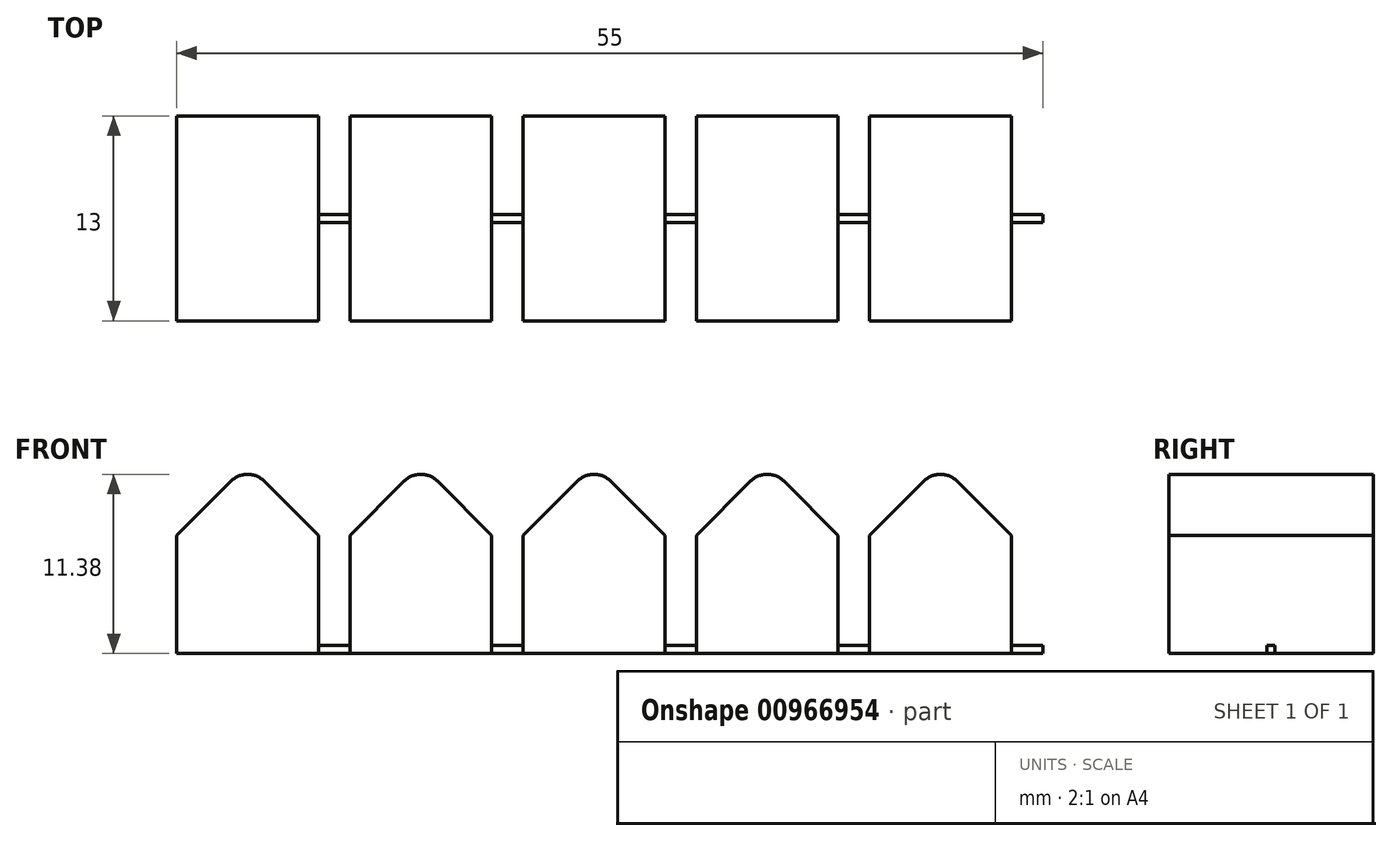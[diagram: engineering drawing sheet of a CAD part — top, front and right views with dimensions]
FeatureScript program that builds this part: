
annotation { "Feature Type Name" : "Feature", "Feature Type Description" : "" }
export const myFeature = defineFeature(function(context is Context, id is Id, definition is map)
    precondition{}
    {
        {
            var Q0;
            Q0=qCreatedBy(makeId("Front.planeOp"),FACE);
            var sketch = newSketch(context, id + "F0", { "sketchPlane" : qUnion([Q0])});
            skLineSegment(sketch, "E0.bottom", {"start": v(4.5, -3.75) * mm, "end": v(-4.5, -3.75) * mm});
            skLineSegment(sketch, "E0.top", {"start": v(4.5, 3.75) * mm, "end": v(-4.5, 3.75) * mm});
            skLineSegment(sketch, "E0.left", {"start": v(4.5, -3.75) * mm, "end": v(4.5, 3.75) * mm});
            skLineSegment(sketch, "E0.right", {"start": v(-4.5, -3.75) * mm, "end": v(-4.5, 3.75) * mm});
            skPoint(sketch, "E0.middle", {"position": v(0, 0) * mm});
            skLineSegment(sketch, "E1", {"start": v(-4.5, 3.75) * mm, "end": v(-1.06, 7.19) * mm});
            skLineSegment(sketch, "E2", {"start": v(1.06, 7.19) * mm, "end": v(4.5, 3.75) * mm});
            skPoint(sketch, "E3.visualSharp", {"position": v(0, 8.25) * mm});
            skArc(sketch, "E3.filletArc", {"start": v(1.06, 7.19) * mm, "mid": v(0, 7.63) * mm, "end": v(-1.06, 7.19) * mm});
            skLineSegment(sketch, "E4.bottom", {"start": v(4.5, -3.75) * mm, "end": v(6.5, -3.75) * mm});
            skLineSegment(sketch, "E4.top", {"start": v(4.5, -3.25) * mm, "end": v(6.5, -3.25) * mm});
            skLineSegment(sketch, "E4.left", {"start": v(4.5, -3.75) * mm, "end": v(4.5, -3.25) * mm});
            skLineSegment(sketch, "E4.right", {"start": v(6.5, -3.75) * mm, "end": v(6.5, -3.25) * mm});
            skLineSegment(sketch, "E5.1.0.0", {"start": v(12.06, 7.19) * mm, "end": v(15.5, 3.75) * mm});
            skLineSegment(sketch, "E5.1.0.1", {"start": v(15.5, -3.75) * mm, "end": v(15.5, 3.75) * mm});
            skLineSegment(sketch, "E5.1.0.2", {"start": v(15.5, -3.75) * mm, "end": v(17.5, -3.75) * mm});
            skLineSegment(sketch, "E5.1.0.3", {"start": v(15.5, 3.75) * mm, "end": v(6.5, 3.75) * mm});
            skPoint(sketch, "E5.1.0.4", {"position": v(11, 8.25) * mm});
            skArc(sketch, "E5.1.0.5", {"start": v(12.06, 7.19) * mm, "mid": v(11, 7.63) * mm, "end": v(9.94, 7.19) * mm});
            skLineSegment(sketch, "E5.1.0.6", {"start": v(15.5, -3.75) * mm, "end": v(6.5, -3.75) * mm});
            skLineSegment(sketch, "E5.1.0.7", {"start": v(15.5, -3.25) * mm, "end": v(17.5, -3.25) * mm});
            skLineSegment(sketch, "E5.1.0.8", {"start": v(6.5, -3.75) * mm, "end": v(6.5, 3.75) * mm});
            skLineSegment(sketch, "E5.1.0.9", {"start": v(6.5, 3.75) * mm, "end": v(9.94, 7.19) * mm});
            skPoint(sketch, "E5.1.0.10", {"position": v(11, 0) * mm});
            skLineSegment(sketch, "E5.1.0.11", {"start": v(15.5, -3.75) * mm, "end": v(15.5, -3.25) * mm});
            skLineSegment(sketch, "E5.1.0.12", {"start": v(17.5, -3.75) * mm, "end": v(17.5, -3.25) * mm});
            skLineSegment(sketch, "E5.2.0.0", {"start": v(23.06, 7.19) * mm, "end": v(26.5, 3.75) * mm});
            skLineSegment(sketch, "E5.2.0.1", {"start": v(26.5, -3.75) * mm, "end": v(26.5, 3.75) * mm});
            skLineSegment(sketch, "E5.2.0.2", {"start": v(26.5, -3.75) * mm, "end": v(28.5, -3.75) * mm});
            skLineSegment(sketch, "E5.2.0.3", {"start": v(26.5, 3.75) * mm, "end": v(17.5, 3.75) * mm});
            skPoint(sketch, "E5.2.0.4", {"position": v(22, 8.25) * mm});
            skArc(sketch, "E5.2.0.5", {"start": v(23.06, 7.19) * mm, "mid": v(22, 7.63) * mm, "end": v(20.94, 7.19) * mm});
            skLineSegment(sketch, "E5.2.0.6", {"start": v(26.5, -3.75) * mm, "end": v(17.5, -3.75) * mm});
            skLineSegment(sketch, "E5.2.0.7", {"start": v(26.5, -3.25) * mm, "end": v(28.5, -3.25) * mm});
            skLineSegment(sketch, "E5.2.0.8", {"start": v(17.5, -3.75) * mm, "end": v(17.5, 3.75) * mm});
            skLineSegment(sketch, "E5.2.0.9", {"start": v(17.5, 3.75) * mm, "end": v(20.94, 7.19) * mm});
            skPoint(sketch, "E5.2.0.10", {"position": v(22, 0) * mm});
            skLineSegment(sketch, "E5.2.0.11", {"start": v(26.5, -3.75) * mm, "end": v(26.5, -3.25) * mm});
            skLineSegment(sketch, "E5.2.0.12", {"start": v(28.5, -3.75) * mm, "end": v(28.5, -3.25) * mm});
            skLineSegment(sketch, "E5.3.0.0", {"start": v(34.06, 7.19) * mm, "end": v(37.5, 3.75) * mm});
            skLineSegment(sketch, "E5.3.0.1", {"start": v(37.5, -3.75) * mm, "end": v(37.5, 3.75) * mm});
            skLineSegment(sketch, "E5.3.0.2", {"start": v(37.5, -3.75) * mm, "end": v(39.5, -3.75) * mm});
            skLineSegment(sketch, "E5.3.0.3", {"start": v(37.5, 3.75) * mm, "end": v(28.5, 3.75) * mm});
            skPoint(sketch, "E5.3.0.4", {"position": v(33, 8.25) * mm});
            skArc(sketch, "E5.3.0.5", {"start": v(34.06, 7.19) * mm, "mid": v(33, 7.63) * mm, "end": v(31.94, 7.19) * mm});
            skLineSegment(sketch, "E5.3.0.6", {"start": v(37.5, -3.75) * mm, "end": v(28.5, -3.75) * mm});
            skLineSegment(sketch, "E5.3.0.7", {"start": v(37.5, -3.25) * mm, "end": v(39.5, -3.25) * mm});
            skLineSegment(sketch, "E5.3.0.8", {"start": v(28.5, -3.75) * mm, "end": v(28.5, 3.75) * mm});
            skLineSegment(sketch, "E5.3.0.9", {"start": v(28.5, 3.75) * mm, "end": v(31.94, 7.19) * mm});
            skPoint(sketch, "E5.3.0.10", {"position": v(33, 0) * mm});
            skLineSegment(sketch, "E5.3.0.11", {"start": v(37.5, -3.75) * mm, "end": v(37.5, -3.25) * mm});
            skLineSegment(sketch, "E5.3.0.12", {"start": v(39.5, -3.75) * mm, "end": v(39.5, -3.25) * mm});
            skLineSegment(sketch, "E5.4.0.0", {"start": v(45.06, 7.19) * mm, "end": v(48.5, 3.75) * mm});
            skLineSegment(sketch, "E5.4.0.1", {"start": v(48.5, -3.75) * mm, "end": v(48.5, 3.75) * mm});
            skLineSegment(sketch, "E5.4.0.2", {"start": v(48.5, -3.75) * mm, "end": v(50.5, -3.75) * mm});
            skLineSegment(sketch, "E5.4.0.3", {"start": v(48.5, 3.75) * mm, "end": v(39.5, 3.75) * mm});
            skPoint(sketch, "E5.4.0.4", {"position": v(44, 8.25) * mm});
            skArc(sketch, "E5.4.0.5", {"start": v(45.06, 7.19) * mm, "mid": v(44, 7.63) * mm, "end": v(42.94, 7.19) * mm});
            skLineSegment(sketch, "E5.4.0.6", {"start": v(48.5, -3.75) * mm, "end": v(39.5, -3.75) * mm});
            skLineSegment(sketch, "E5.4.0.7", {"start": v(48.5, -3.25) * mm, "end": v(50.5, -3.25) * mm});
            skLineSegment(sketch, "E5.4.0.8", {"start": v(39.5, -3.75) * mm, "end": v(39.5, 3.75) * mm});
            skLineSegment(sketch, "E5.4.0.9", {"start": v(39.5, 3.75) * mm, "end": v(42.94, 7.19) * mm});
            skPoint(sketch, "E5.4.0.10", {"position": v(44, 0) * mm});
            skLineSegment(sketch, "E5.4.0.11", {"start": v(48.5, -3.75) * mm, "end": v(48.5, -3.25) * mm});
            skLineSegment(sketch, "E5.4.0.12", {"start": v(50.5, -3.75) * mm, "end": v(50.5, -3.25) * mm});
            skLineSegment(sketch, "E5.direction1", {"start": v(-4.5, -3.75) * mm, "end": v(6.5, -3.75) * mm, "construction": true});
            skSolve(sketch);
        }
        {
            var Q0;
            Q0 = qSketchRegion(id + "F0", true);
            extrude(context, id + "F1", {"entities" : qUnion([Q0]), "oppositeDirection" : true, "depth" : 13 * mm, "offsetDistance" : 25 * mm});
        }
        {
            var Q0;
            Q0=makeQuery(id+"F1.opExtrude","SWEPT_FACE",FACE,{"disambiguationData":[OSD([sQuery(id+"F0.wireOp",EDGE,"E0.bottom"),sQuery(id+"F0.wireOp",EDGE,"E4.bottom"),sQuery(id+"F0.wireOp",EDGE,"E5.1.0.2"),sQuery(id+"F0.wireOp",EDGE,"E5.1.0.6"),sQuery(id+"F0.wireOp",EDGE,"E5.2.0.2"),sQuery(id+"F0.wireOp",EDGE,"E5.2.0.6"),sQuery(id+"F0.wireOp",EDGE,"E5.3.0.2"),sQuery(id+"F0.wireOp",EDGE,"E5.3.0.6"),sQuery(id+"F0.wireOp",EDGE,"E5.4.0.2"),sQuery(id+"F0.wireOp",EDGE,"E5.4.0.6")])]});
            var sketch = newSketch(context, id + "F2", { "sketchPlane" : qUnion([Q0])});
            skPoint(sketch, "E6", {"position": v(4.5, 0) * mm});
            skLineSegment(sketch, "E7.bottom", {"start": v(4.5, 0) * mm, "end": v(6.5, 0) * mm});
            skLineSegment(sketch, "E7.top", {"start": v(4.5, -6.25) * mm, "end": v(6.5, -6.25) * mm});
            skLineSegment(sketch, "E7.left", {"start": v(4.5, 0) * mm, "end": v(4.5, -6.25) * mm});
            skLineSegment(sketch, "E7.right", {"start": v(6.5, 0) * mm, "end": v(6.5, -6.25) * mm});
            skLineSegment(sketch, "E8.0.1.0", {"start": v(4.5, -6.75) * mm, "end": v(6.5, -6.75) * mm});
            skLineSegment(sketch, "E8.0.1.1", {"start": v(6.5, -6.75) * mm, "end": v(6.5, -13) * mm});
            skPoint(sketch, "E8.0.1.2", {"position": v(4.5, -6.75) * mm});
            skLineSegment(sketch, "E8.0.1.3", {"start": v(4.5, -6.75) * mm, "end": v(4.5, -13) * mm});
            skLineSegment(sketch, "E8.0.1.4", {"start": v(4.5, -13) * mm, "end": v(6.5, -13) * mm});
            skLineSegment(sketch, "E8.1.0.0", {"start": v(15.5, 0) * mm, "end": v(17.5, 0) * mm});
            skLineSegment(sketch, "E8.1.0.1", {"start": v(17.5, 0) * mm, "end": v(17.5, -6.25) * mm});
            skPoint(sketch, "E8.1.0.2", {"position": v(15.5, 0) * mm});
            skLineSegment(sketch, "E8.1.0.3", {"start": v(15.5, 0) * mm, "end": v(15.5, -6.25) * mm});
            skLineSegment(sketch, "E8.1.0.4", {"start": v(15.5, -6.25) * mm, "end": v(17.5, -6.25) * mm});
            skLineSegment(sketch, "E8.1.1.0", {"start": v(15.5, -6.75) * mm, "end": v(17.5, -6.75) * mm});
            skLineSegment(sketch, "E8.1.1.1", {"start": v(17.5, -6.75) * mm, "end": v(17.5, -13) * mm});
            skPoint(sketch, "E8.1.1.2", {"position": v(15.5, -6.75) * mm});
            skLineSegment(sketch, "E8.1.1.3", {"start": v(15.5, -6.75) * mm, "end": v(15.5, -13) * mm});
            skLineSegment(sketch, "E8.1.1.4", {"start": v(15.5, -13) * mm, "end": v(17.5, -13) * mm});
            skLineSegment(sketch, "E8.2.0.0", {"start": v(26.5, 0) * mm, "end": v(28.5, 0) * mm});
            skLineSegment(sketch, "E8.2.0.1", {"start": v(28.5, 0) * mm, "end": v(28.5, -6.25) * mm});
            skPoint(sketch, "E8.2.0.2", {"position": v(26.5, 0) * mm});
            skLineSegment(sketch, "E8.2.0.3", {"start": v(26.5, 0) * mm, "end": v(26.5, -6.25) * mm});
            skLineSegment(sketch, "E8.2.0.4", {"start": v(26.5, -6.25) * mm, "end": v(28.5, -6.25) * mm});
            skLineSegment(sketch, "E8.2.1.0", {"start": v(26.5, -6.75) * mm, "end": v(28.5, -6.75) * mm});
            skLineSegment(sketch, "E8.2.1.1", {"start": v(28.5, -6.75) * mm, "end": v(28.5, -13) * mm});
            skPoint(sketch, "E8.2.1.2", {"position": v(26.5, -6.75) * mm});
            skLineSegment(sketch, "E8.2.1.3", {"start": v(26.5, -6.75) * mm, "end": v(26.5, -13) * mm});
            skLineSegment(sketch, "E8.2.1.4", {"start": v(26.5, -13) * mm, "end": v(28.5, -13) * mm});
            skLineSegment(sketch, "E8.3.0.0", {"start": v(37.5, 0) * mm, "end": v(39.5, 0) * mm});
            skLineSegment(sketch, "E8.3.0.1", {"start": v(39.5, 0) * mm, "end": v(39.5, -6.25) * mm});
            skPoint(sketch, "E8.3.0.2", {"position": v(37.5, 0) * mm});
            skLineSegment(sketch, "E8.3.0.3", {"start": v(37.5, 0) * mm, "end": v(37.5, -6.25) * mm});
            skLineSegment(sketch, "E8.3.0.4", {"start": v(37.5, -6.25) * mm, "end": v(39.5, -6.25) * mm});
            skLineSegment(sketch, "E8.3.1.0", {"start": v(37.5, -6.75) * mm, "end": v(39.5, -6.75) * mm});
            skLineSegment(sketch, "E8.3.1.1", {"start": v(39.5, -6.75) * mm, "end": v(39.5, -13) * mm});
            skPoint(sketch, "E8.3.1.2", {"position": v(37.5, -6.75) * mm});
            skLineSegment(sketch, "E8.3.1.3", {"start": v(37.5, -6.75) * mm, "end": v(37.5, -13) * mm});
            skLineSegment(sketch, "E8.3.1.4", {"start": v(37.5, -13) * mm, "end": v(39.5, -13) * mm});
            skLineSegment(sketch, "E8.4.0.0", {"start": v(48.5, 0) * mm, "end": v(50.5, 0) * mm});
            skLineSegment(sketch, "E8.4.0.1", {"start": v(50.5, 0) * mm, "end": v(50.5, -6.25) * mm});
            skPoint(sketch, "E8.4.0.2", {"position": v(48.5, 0) * mm});
            skLineSegment(sketch, "E8.4.0.3", {"start": v(48.5, 0) * mm, "end": v(48.5, -6.25) * mm});
            skLineSegment(sketch, "E8.4.0.4", {"start": v(48.5, -6.25) * mm, "end": v(50.5, -6.25) * mm});
            skLineSegment(sketch, "E8.4.1.0", {"start": v(48.5, -6.75) * mm, "end": v(50.5, -6.75) * mm});
            skLineSegment(sketch, "E8.4.1.1", {"start": v(50.5, -6.75) * mm, "end": v(50.5, -13) * mm});
            skPoint(sketch, "E8.4.1.2", {"position": v(48.5, -6.75) * mm});
            skLineSegment(sketch, "E8.4.1.3", {"start": v(48.5, -6.75) * mm, "end": v(48.5, -13) * mm});
            skLineSegment(sketch, "E8.4.1.4", {"start": v(48.5, -13) * mm, "end": v(50.5, -13) * mm});
            skLineSegment(sketch, "E8.direction1", {"start": v(4.5, -6.25) * mm, "end": v(15.5, -6.25) * mm, "construction": true});
            skLineSegment(sketch, "E8.direction2", {"start": v(4.5, -6.25) * mm, "end": v(4.5, -13) * mm, "construction": true});
            skSolve(sketch);
        }
        {
            var Q0;
            Q0 = qSketchRegion(id + "F2", true);
            extrude(context, id + "F3", {"entities" : qUnion([Q0]), "operationType" : NewBodyOperationType.REMOVE, "endBound" : BoundingType.THROUGH_ALL, "oppositeDirection" : true, "depth" : 25 * mm, "offsetDistance" : 25 * mm});
        }
    });
